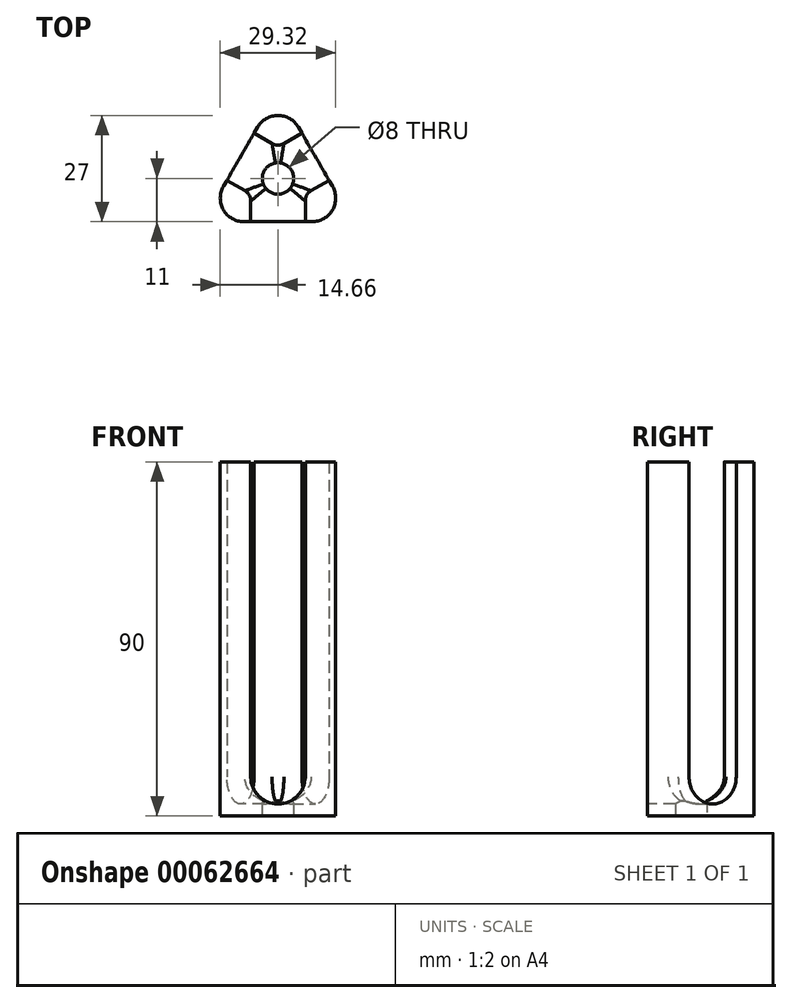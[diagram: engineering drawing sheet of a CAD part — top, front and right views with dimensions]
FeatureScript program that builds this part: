
annotation { "Feature Type Name" : "Feature", "Feature Type Description" : "" }
export const myFeature = defineFeature(function(context is Context, id is Id, definition is map)
    precondition{}
    {
        {
            var Q0;
            Q0=qCreatedBy(makeId("Top.planeOp"),FACE);
            var sketch = newSketch(context, id + "F0", { "sketchPlane" : qUnion([Q0])});
            skCircle(sketch, "E0.cCircle", {"center": v(0, 0) * mm, "radius": 11 * mm, "construction": true});
            skLineSegment(sketch, "E0.0", {"start": v(8.66, -11) * mm, "end": v(-8.66, -11) * mm});
            skLineSegment(sketch, "E0.1", {"start": v(-13.86, -2) * mm, "end": v(-5.2, 13) * mm});
            skLineSegment(sketch, "E0.2", {"start": v(5.2, 13) * mm, "end": v(13.86, -2) * mm});
            skPoint(sketch, "E1.visualSharp", {"position": v(0, 22) * mm});
            skArc(sketch, "E1.filletArc", {"start": v(5.2, 13) * mm, "mid": v(0, 16) * mm, "end": v(-5.2, 13) * mm});
            skPoint(sketch, "E2.visualSharp", {"position": v(-19.05, -11) * mm});
            skArc(sketch, "E2.filletArc", {"start": v(-13.86, -2) * mm, "mid": v(-13.86, -8) * mm, "end": v(-8.66, -11) * mm});
            skPoint(sketch, "E3.visualSharp", {"position": v(19.05, -11) * mm});
            skArc(sketch, "E3.filletArc", {"start": v(8.66, -11) * mm, "mid": v(13.86, -8) * mm, "end": v(13.86, -2) * mm});
            skCircle(sketch, "E4", {"center": v(0, 0) * mm, "radius": 16 * mm, "construction": true});
            skLineSegment(sketch, "E5.trimOffspring", {"start": v(0, 8) * mm, "end": v(6.06, 11.5) * mm});
            skLineSegment(sketch, "E6.trimOffspring", {"start": v(0, 8) * mm, "end": v(-6.06, 11.5) * mm});
            skLineSegment(sketch, "E7.trimOffspring", {"start": v(6.93, -4) * mm, "end": v(13, -0.5) * mm});
            skLineSegment(sketch, "E8.trimOffspring", {"start": v(-6.93, -4) * mm, "end": v(-13, -0.5) * mm});
            skLineSegment(sketch, "E9.trimOffspring", {"start": v(-6.93, -4) * mm, "end": v(-6.93, -11) * mm});
            skLineSegment(sketch, "E10.trimOffspring", {"start": v(6.93, -4) * mm, "end": v(6.93, -11) * mm});
            skSolve(sketch);
        }
        {
            var Q0;
            {var subQ1=sQuery(id+"F0.wireOp",EDGE,"E3.filletArc");Q0=makeQuery(id+"F0.imprint","IMPRINT",FACE,{"disambiguationData":[TD([[makeQuery(id+"F0.imprint","IMPRINT",EDGE,{"derivedFrom":subQ1}),1.0]])]});}
            var Q1;
            {var subQ1=sQuery(id+"F0.wireOp",EDGE,"E2.filletArc");Q1=makeQuery(id+"F0.imprint","IMPRINT",FACE,{"disambiguationData":[TD([[makeQuery(id+"F0.imprint","IMPRINT",EDGE,{"derivedFrom":subQ1}),1.0]])]});}
            var Q2;
            {var subQ1=sQuery(id+"F0.wireOp",EDGE,"E3.filletArc");Q2=makeQuery(id+"F0.imprint","IMPRINT",FACE,{"disambiguationData":[TD([[makeQuery(id+"F0.imprint","IMPRINT",EDGE,{"derivedFrom":subQ1}),1.0]])]});}
            var Q3;
            {var subQ1=sQuery(id+"F0.wireOp",EDGE,"E2.filletArc");Q3=makeQuery(id+"F0.imprint","IMPRINT",FACE,{"disambiguationData":[TD([[makeQuery(id+"F0.imprint","IMPRINT",EDGE,{"derivedFrom":subQ1}),1.0]])]});}
            var Q4;
            {var subQ1=sQuery(id+"F0.wireOp",EDGE,"E1.filletArc");Q4=makeQuery(id+"F0.imprint","IMPRINT",FACE,{"disambiguationData":[TD([[makeQuery(id+"F0.imprint","IMPRINT",EDGE,{"derivedFrom":subQ1}),1.0]])]});}
            extrude(context, id + "F1", {"entities" : qUnion([Q0, Q1, Q2, Q3, Q4]), "depth" : 90 * mm});
        }
        {
            var Q0;
            Q0=qCreatedBy(makeId("Top.planeOp"),FACE);
            var sketch = newSketch(context, id + "F2", { "sketchPlane" : qUnion([Q0])});
            skCircle(sketch, "E11.cCircle", {"center": v(0, 0) * mm, "radius": 11 * mm, "construction": true});
            skLineSegment(sketch, "E11.0", {"start": v(8.66, -11) * mm, "end": v(-8.66, -11) * mm});
            skLineSegment(sketch, "E11.1", {"start": v(-13.86, -2) * mm, "end": v(-5.2, 13) * mm});
            skLineSegment(sketch, "E11.2", {"start": v(5.2, 13) * mm, "end": v(13.86, -2) * mm});
            skPoint(sketch, "E12.visualSharp", {"position": v(0, 22) * mm});
            skArc(sketch, "E12.filletArc", {"start": v(5.2, 13) * mm, "mid": v(0, 16) * mm, "end": v(-5.2, 13) * mm});
            skPoint(sketch, "E13.visualSharp", {"position": v(-19.05, -11) * mm});
            skArc(sketch, "E13.filletArc", {"start": v(-13.86, -2) * mm, "mid": v(-13.86, -8) * mm, "end": v(-8.66, -11) * mm});
            skPoint(sketch, "E14.visualSharp", {"position": v(19.05, -11) * mm});
            skArc(sketch, "E14.filletArc", {"start": v(8.66, -11) * mm, "mid": v(13.86, -8) * mm, "end": v(13.86, -2) * mm});
            skCircle(sketch, "E15", {"center": v(0, 0) * mm, "radius": 16 * mm, "construction": true});
            skSolve(sketch);
        }
        {
            var Q0;
            Q0 = qSketchRegion(id + "F2", true);
            extrude(context, id + "F3", {"entities" : qUnion([Q0]), "operationType" : NewBodyOperationType.ADD, "depth" : 1 * mm});
        }
        {
            var Q0;
            Q0=makeQuery(id+"F1.opExtrude","SWEPT_EDGE",EDGE,{"disambiguationData":[OSD([sQuery(id+"F0.wireOp",EDGE,"E8.trimOffspring"),sQuery(id+"F0.wireOp",EDGE,"E9.trimOffspring")])]});
            var Q1;
            Q1=makeQuery(id+"F1.opExtrude","SWEPT_EDGE",EDGE,{"disambiguationData":[OSD([sQuery(id+"F0.wireOp",EDGE,"E7.trimOffspring"),sQuery(id+"F0.wireOp",EDGE,"E10.trimOffspring")])]});
            var Q2;
            Q2=makeQuery(id+"F1.opExtrude","SWEPT_EDGE",EDGE,{"disambiguationData":[OSD([sQuery(id+"F0.wireOp",EDGE,"E5.trimOffspring"),sQuery(id+"F0.wireOp",EDGE,"E6.trimOffspring")])]});
            fillet(context, id + "F4", {"entities" : qUnion([Q0, Q1, Q2]), "radius" : 3 * mm, "tangentPropagation" : true, "allowEdgeOverflow" : false});
        }
        {
            var Q0;
            {var subQ0=sQuery(id+"F0.wireOp",EDGE,"E0.2");var subQ1=sQuery(id+"F0.wireOp",EDGE,"E0.1");var subQ2=sQuery(id+"F0.wireOp",EDGE,"E0.0");Q0=makeQuery(id+"F3.boolean.opBoolean","MERGE",FACE,{"derivedFrom":[makeQuery(id+"F1.opExtrude","CAP_FACE",FACE,{"disambiguationData":[OSD([subQ2,subQ0,sQuery(id+"F0.wireOp",EDGE,"E3.filletArc"),sQuery(id+"F0.wireOp",EDGE,"E7.trimOffspring"),sQuery(id+"F0.wireOp",EDGE,"E10.trimOffspring")])],"isStart":true}),makeQuery(id+"F1.opExtrude","CAP_FACE",FACE,{"disambiguationData":[OSD([subQ2,subQ1,sQuery(id+"F0.wireOp",EDGE,"E2.filletArc"),sQuery(id+"F0.wireOp",EDGE,"E8.trimOffspring"),sQuery(id+"F0.wireOp",EDGE,"E9.trimOffspring")])],"isStart":true}),makeQuery(id+"F1.opExtrude","CAP_FACE",FACE,{"disambiguationData":[OSD([subQ1,subQ0,sQuery(id+"F0.wireOp",EDGE,"E1.filletArc"),sQuery(id+"F0.wireOp",EDGE,"E5.trimOffspring"),sQuery(id+"F0.wireOp",EDGE,"E6.trimOffspring")])],"isStart":true}),makeQuery(id+"F3.opExtrude","CAP_FACE",FACE,{"disambiguationData":[OSD([sQuery(id+"F2.wireOp",EDGE,"E11.0"),sQuery(id+"F2.wireOp",EDGE,"E11.1"),sQuery(id+"F2.wireOp",EDGE,"E11.2"),sQuery(id+"F2.wireOp",EDGE,"E12.filletArc"),sQuery(id+"F2.wireOp",EDGE,"E13.filletArc"),sQuery(id+"F2.wireOp",EDGE,"E14.filletArc")])],"isStart":true})]});}
            var sketch = newSketch(context, id + "F5", { "sketchPlane" : qUnion([Q0])});
            skSolve(sketch);
        }
        {
            var Q0;
            {var subQ0=sQuery(id+"F0.wireOp",EDGE,"E0.2");var subQ1=sQuery(id+"F0.wireOp",EDGE,"E0.1");var subQ2=sQuery(id+"F0.wireOp",EDGE,"E0.0");Q0=makeQuery(id+"F3.boolean.opBoolean","MERGE",FACE,{"derivedFrom":[makeQuery(id+"F1.opExtrude","CAP_FACE",FACE,{"disambiguationData":[OSD([subQ2,subQ0,sQuery(id+"F0.wireOp",EDGE,"E3.filletArc"),sQuery(id+"F0.wireOp",EDGE,"E7.trimOffspring"),sQuery(id+"F0.wireOp",EDGE,"E10.trimOffspring")])],"isStart":true}),makeQuery(id+"F1.opExtrude","CAP_FACE",FACE,{"disambiguationData":[OSD([subQ2,subQ1,sQuery(id+"F0.wireOp",EDGE,"E2.filletArc"),sQuery(id+"F0.wireOp",EDGE,"E8.trimOffspring"),sQuery(id+"F0.wireOp",EDGE,"E9.trimOffspring")])],"isStart":true}),makeQuery(id+"F1.opExtrude","CAP_FACE",FACE,{"disambiguationData":[OSD([subQ1,subQ0,sQuery(id+"F0.wireOp",EDGE,"E1.filletArc"),sQuery(id+"F0.wireOp",EDGE,"E5.trimOffspring"),sQuery(id+"F0.wireOp",EDGE,"E6.trimOffspring")])],"isStart":true}),makeQuery(id+"F3.opExtrude","CAP_FACE",FACE,{"disambiguationData":[OSD([sQuery(id+"F2.wireOp",EDGE,"E11.0"),sQuery(id+"F2.wireOp",EDGE,"E11.1"),sQuery(id+"F2.wireOp",EDGE,"E11.2"),sQuery(id+"F2.wireOp",EDGE,"E12.filletArc"),sQuery(id+"F2.wireOp",EDGE,"E13.filletArc"),sQuery(id+"F2.wireOp",EDGE,"E14.filletArc")])],"isStart":true})]});}
            var Q1;
            {var subQ3=sQuery(id+"F0.wireOp",EDGE,"E1.filletArc");Q1=makeQuery(id+"F5.imprint","IMPRINT",FACE,{"disambiguationData":[TD([[makeQuery(id+"F5.imprint","IMPRINT",EDGE,{"derivedFrom":makeQuery(id+"F1.opExtrude","CAP_EDGE",EDGE,{"disambiguationData":[OSD([subQ3])],"isStart":true})}),-1.0]])]});}
            extrude(context, id + "F6", {"entities" : qUnion([Q0, Q1]), "operationType" : NewBodyOperationType.ADD, "oppositeDirection" : true, "depth" : 10 * mm});
        }
        {
            var Q0;
            {var subQ0=sQuery(id+"F2.wireOp",EDGE,"E11.0");var subQ1=sQuery(id+"F0.wireOp",EDGE,"E0.0");var subQ2=makeQuery(id+"F0.imprint","IMPRINT",EDGE,{"disambiguationData":[TD([[makeQuery(id+"F0.imprint","INTERSECT",VERTEX,{"derivedFrom":[subQ1,sQuery(id+"F0.wireOp",EDGE,"E2.filletArc")]}),1.0]])],"derivedFrom":subQ1});var subQ3=makeQuery(id+"F0.imprint","IMPRINT",EDGE,{"disambiguationData":[TD([[makeQuery(id+"F0.imprint","INTERSECT",VERTEX,{"derivedFrom":[subQ1,sQuery(id+"F0.wireOp",EDGE,"E3.filletArc")]}),-1.0]])],"derivedFrom":subQ1});Q0=makeQuery(id+"F6.boolean.opBoolean","MERGE",FACE,{"derivedFrom":[makeQuery(id+"F3.boolean.opBoolean","MERGE",FACE,{"derivedFrom":[makeQuery(id+"F1.opExtrude","SWEPT_FACE",FACE,{"disambiguationData":[OSD([subQ1]),TDD([subQ3])]}),makeQuery(id+"F1.opExtrude","SWEPT_FACE",FACE,{"disambiguationData":[OSD([subQ1]),TDD([subQ2])]}),makeQuery(id+"F3.opExtrude","SWEPT_FACE",FACE,{"disambiguationData":[OSD([subQ0])]})]}),makeQuery(id+"F6.opExtrude","SWEPT_FACE",FACE,{"disambiguationData":[OSD([subQ1,subQ0]),TDD([makeQuery(id+"F3.boolean.opBoolean","MERGE",EDGE,{"derivedFrom":[makeQuery(id+"F1.opExtrude","CAP_EDGE",EDGE,{"disambiguationData":[OSD([subQ1]),TDD([subQ3])],"isStart":true}),makeQuery(id+"F1.opExtrude","CAP_EDGE",EDGE,{"disambiguationData":[OSD([subQ1]),TDD([subQ2])],"isStart":true}),makeQuery(id+"F3.opExtrude","CAP_EDGE",EDGE,{"disambiguationData":[OSD([subQ0])],"isStart":true})]})])]})]});}
            var sketch = newSketch(context, id + "F7", { "sketchPlane" : qUnion([Q0])});
            skLineSegment(sketch, "E16.0", {"start": v(6.93, 10) * mm, "end": v(-6.93, 10) * mm});
            skCircle(sketch, "E17", {"center": v(0, 10) * mm, "radius": 6.93 * mm});
            skSolve(sketch);
        }
        {
            var Q0;
            Q0 = qSketchRegion(id + "F7", true);
            extrude(context, id + "F8", {"entities" : qUnion([Q0]), "operationType" : NewBodyOperationType.REMOVE, "oppositeDirection" : true, "depth" : 10 * mm});
        }
        {
            var Q0;
            {var subQ0=sQuery(id+"F2.wireOp",EDGE,"E11.1");var subQ1=sQuery(id+"F0.wireOp",EDGE,"E0.1");var subQ2=makeQuery(id+"F0.imprint","IMPRINT",EDGE,{"disambiguationData":[TD([[makeQuery(id+"F0.imprint","INTERSECT",VERTEX,{"derivedFrom":[subQ1,sQuery(id+"F0.wireOp",EDGE,"E1.filletArc")]}),1.0]])],"derivedFrom":subQ1});var subQ3=makeQuery(id+"F0.imprint","IMPRINT",EDGE,{"disambiguationData":[TD([[makeQuery(id+"F0.imprint","INTERSECT",VERTEX,{"derivedFrom":[subQ1,sQuery(id+"F0.wireOp",EDGE,"E2.filletArc")]}),-1.0]])],"derivedFrom":subQ1});Q0=makeQuery(id+"F6.boolean.opBoolean","MERGE",FACE,{"derivedFrom":[makeQuery(id+"F3.boolean.opBoolean","MERGE",FACE,{"derivedFrom":[makeQuery(id+"F1.opExtrude","SWEPT_FACE",FACE,{"disambiguationData":[OSD([subQ1]),TDD([subQ3])]}),makeQuery(id+"F1.opExtrude","SWEPT_FACE",FACE,{"disambiguationData":[OSD([subQ1]),TDD([subQ2])]}),makeQuery(id+"F3.opExtrude","SWEPT_FACE",FACE,{"disambiguationData":[OSD([subQ0])]})]}),makeQuery(id+"F6.opExtrude","SWEPT_FACE",FACE,{"disambiguationData":[OSD([subQ1,subQ0]),TDD([makeQuery(id+"F3.boolean.opBoolean","MERGE",EDGE,{"derivedFrom":[makeQuery(id+"F1.opExtrude","CAP_EDGE",EDGE,{"disambiguationData":[OSD([subQ1]),TDD([subQ3])],"isStart":true}),makeQuery(id+"F1.opExtrude","CAP_EDGE",EDGE,{"disambiguationData":[OSD([subQ1]),TDD([subQ2])],"isStart":true}),makeQuery(id+"F3.opExtrude","CAP_EDGE",EDGE,{"disambiguationData":[OSD([subQ0])],"isStart":true})]})])]})]});}
            var sketch = newSketch(context, id + "F9", { "sketchPlane" : qUnion([Q0])});
            skLineSegment(sketch, "E18.0", {"start": v(6.93, 10) * mm, "end": v(-6.93, 10) * mm});
            skCircle(sketch, "E19", {"center": v(0, 10) * mm, "radius": 6.93 * mm});
            skSolve(sketch);
        }
        {
            var Q0;
            Q0 = qSketchRegion(id + "F9", true);
            extrude(context, id + "F10", {"entities" : qUnion([Q0]), "operationType" : NewBodyOperationType.REMOVE, "oppositeDirection" : true, "depth" : 10 * mm});
        }
        {
            var Q0;
            {var subQ0=sQuery(id+"F2.wireOp",EDGE,"E11.2");var subQ1=sQuery(id+"F0.wireOp",EDGE,"E0.2");var subQ2=makeQuery(id+"F0.imprint","IMPRINT",EDGE,{"disambiguationData":[TD([[makeQuery(id+"F0.imprint","INTERSECT",VERTEX,{"derivedFrom":[subQ1,sQuery(id+"F0.wireOp",EDGE,"E3.filletArc")]}),1.0]])],"derivedFrom":subQ1});var subQ3=makeQuery(id+"F0.imprint","IMPRINT",EDGE,{"disambiguationData":[TD([[makeQuery(id+"F0.imprint","INTERSECT",VERTEX,{"derivedFrom":[subQ1,sQuery(id+"F0.wireOp",EDGE,"E1.filletArc")]}),-1.0]])],"derivedFrom":subQ1});Q0=makeQuery(id+"F6.boolean.opBoolean","MERGE",FACE,{"derivedFrom":[makeQuery(id+"F3.boolean.opBoolean","MERGE",FACE,{"derivedFrom":[makeQuery(id+"F1.opExtrude","SWEPT_FACE",FACE,{"disambiguationData":[OSD([subQ1]),TDD([subQ3])]}),makeQuery(id+"F1.opExtrude","SWEPT_FACE",FACE,{"disambiguationData":[OSD([subQ1]),TDD([subQ2])]}),makeQuery(id+"F3.opExtrude","SWEPT_FACE",FACE,{"disambiguationData":[OSD([subQ0])]})]}),makeQuery(id+"F6.opExtrude","SWEPT_FACE",FACE,{"disambiguationData":[OSD([subQ1,subQ0]),TDD([makeQuery(id+"F3.boolean.opBoolean","MERGE",EDGE,{"derivedFrom":[makeQuery(id+"F1.opExtrude","CAP_EDGE",EDGE,{"disambiguationData":[OSD([subQ1]),TDD([subQ3])],"isStart":true}),makeQuery(id+"F1.opExtrude","CAP_EDGE",EDGE,{"disambiguationData":[OSD([subQ1]),TDD([subQ2])],"isStart":true}),makeQuery(id+"F3.opExtrude","CAP_EDGE",EDGE,{"disambiguationData":[OSD([subQ0])],"isStart":true})]})])]})]});}
            var sketch = newSketch(context, id + "F11", { "sketchPlane" : qUnion([Q0])});
            skLineSegment(sketch, "E20.0", {"start": v(6.93, 10) * mm, "end": v(-6.93, 10) * mm});
            skCircle(sketch, "E21", {"center": v(0, 10) * mm, "radius": 6.93 * mm});
            skSolve(sketch);
        }
        {
            var Q0;
            Q0 = qSketchRegion(id + "F11", true);
            extrude(context, id + "F12", {"entities" : qUnion([Q0]), "operationType" : NewBodyOperationType.REMOVE, "oppositeDirection" : true, "depth" : 10 * mm});
        }
        {
            var Q0;
            Q0=makeQuery(id+"F10.boolean.opBoolean","INTERSECT",EDGE,{"derivedFrom":[makeQuery(id+"F8.boolean.opBoolean","COPY",FACE,{"derivedFrom":makeQuery(id+"F8.opExtrude","SWEPT_FACE",FACE,{"disambiguationData":[OSD([sQuery(id+"F7.wireOp",EDGE,"E17")])]})}),makeQuery(id+"F10.opExtrude","SWEPT_FACE",FACE,{"disambiguationData":[OSD([sQuery(id+"F9.wireOp",EDGE,"E19")])]})]});
            var Q1;
            Q1=makeQuery(id+"F12.boolean.opBoolean","INTERSECT",EDGE,{"derivedFrom":[makeQuery(id+"F8.boolean.opBoolean","COPY",FACE,{"derivedFrom":makeQuery(id+"F8.opExtrude","SWEPT_FACE",FACE,{"disambiguationData":[OSD([sQuery(id+"F7.wireOp",EDGE,"E17")])]})}),makeQuery(id+"F12.opExtrude","SWEPT_FACE",FACE,{"disambiguationData":[OSD([sQuery(id+"F11.wireOp",EDGE,"E21")])]})]});
            var Q2;
            Q2=makeQuery(id+"F12.boolean.opBoolean","INTERSECT",EDGE,{"derivedFrom":[makeQuery(id+"F10.boolean.opBoolean","COPY",FACE,{"derivedFrom":makeQuery(id+"F10.opExtrude","SWEPT_FACE",FACE,{"disambiguationData":[OSD([sQuery(id+"F9.wireOp",EDGE,"E19")])]})}),makeQuery(id+"F12.opExtrude","SWEPT_FACE",FACE,{"disambiguationData":[OSD([sQuery(id+"F11.wireOp",EDGE,"E21")])]})]});
            fillet(context, id + "F13", {"entities" : qUnion([Q0, Q1, Q2]), "radius" : 3 * mm, "tangentPropagation" : true, "allowEdgeOverflow" : false});
        }
        {
            var Q0;
            {var subQ0=sQuery(id+"F0.wireOp",EDGE,"E0.2");var subQ1=sQuery(id+"F0.wireOp",EDGE,"E0.1");var subQ2=sQuery(id+"F0.wireOp",EDGE,"E0.0");Q0=makeQuery(id+"F3.boolean.opBoolean","MERGE",FACE,{"derivedFrom":[makeQuery(id+"F1.opExtrude","CAP_FACE",FACE,{"disambiguationData":[OSD([subQ2,subQ0,sQuery(id+"F0.wireOp",EDGE,"E3.filletArc"),sQuery(id+"F0.wireOp",EDGE,"E7.trimOffspring"),sQuery(id+"F0.wireOp",EDGE,"E10.trimOffspring")])],"isStart":true}),makeQuery(id+"F1.opExtrude","CAP_FACE",FACE,{"disambiguationData":[OSD([subQ2,subQ1,sQuery(id+"F0.wireOp",EDGE,"E2.filletArc"),sQuery(id+"F0.wireOp",EDGE,"E8.trimOffspring"),sQuery(id+"F0.wireOp",EDGE,"E9.trimOffspring")])],"isStart":true}),makeQuery(id+"F1.opExtrude","CAP_FACE",FACE,{"disambiguationData":[OSD([subQ1,subQ0,sQuery(id+"F0.wireOp",EDGE,"E1.filletArc"),sQuery(id+"F0.wireOp",EDGE,"E5.trimOffspring"),sQuery(id+"F0.wireOp",EDGE,"E6.trimOffspring")])],"isStart":true}),makeQuery(id+"F3.opExtrude","CAP_FACE",FACE,{"disambiguationData":[OSD([sQuery(id+"F2.wireOp",EDGE,"E11.0"),sQuery(id+"F2.wireOp",EDGE,"E11.1"),sQuery(id+"F2.wireOp",EDGE,"E11.2"),sQuery(id+"F2.wireOp",EDGE,"E12.filletArc"),sQuery(id+"F2.wireOp",EDGE,"E13.filletArc"),sQuery(id+"F2.wireOp",EDGE,"E14.filletArc")])],"isStart":true})]});}
            var sketch = newSketch(context, id + "F14", { "sketchPlane" : qUnion([Q0])});
            skCircle(sketch, "E22", {"center": v(0, 0) * mm, "radius": 4 * mm});
            skSolve(sketch);
        }
        {
            var Q0;
            Q0 = qSketchRegion(id + "F14", true);
            extrude(context, id + "F15", {"entities" : qUnion([Q0]), "operationType" : NewBodyOperationType.REMOVE, "oppositeDirection" : true, "depth" : 25 * mm});
        }
    });
